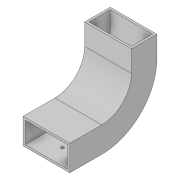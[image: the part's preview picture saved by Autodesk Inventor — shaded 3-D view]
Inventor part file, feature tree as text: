
AUTODESK INVENTOR PART (.ipt)
format: ipt  version: 2018.2 (Build 222227000, 227)  size: 119,296 bytes
history: native  units: in
note: dims shown in document units (in); Inventor stores cm internally (conversion verified against a paired STEP export)
features: sketch x9, sweep x2, plane x1
ambient origin geometry x8: Origin, YZ Plane, XZ Plane, XY Plane, X Axis, Y Axis, Z Axis, Center Point
bodies: Solid1 (feature_tree)
feature tree (12):
  sketch  "Sketch1"  dims[d0=3.937in d1=1.9685in]
  sweep  "Sweep1"
  sketch  "Sketch6"  dims[d21=60.0deg]
  sketch  "3D Sketch1"
  plane  "Work Plane6"
  sketch  "Sketch7"  dims[d22=0.2756in]
  sketch  "Sketch8"  dims[d23=0.0in d24=0.0in]
  sketch  "Sketch9"
  sweep  "Sweep2"
  sketch  "Sketch2"  dims[d2=4.3307in d3=2.3622in]
  sketch  "Sketch3"  dims[d7=0.0in d8=0.0in]
  sketch  "Sketch10"
